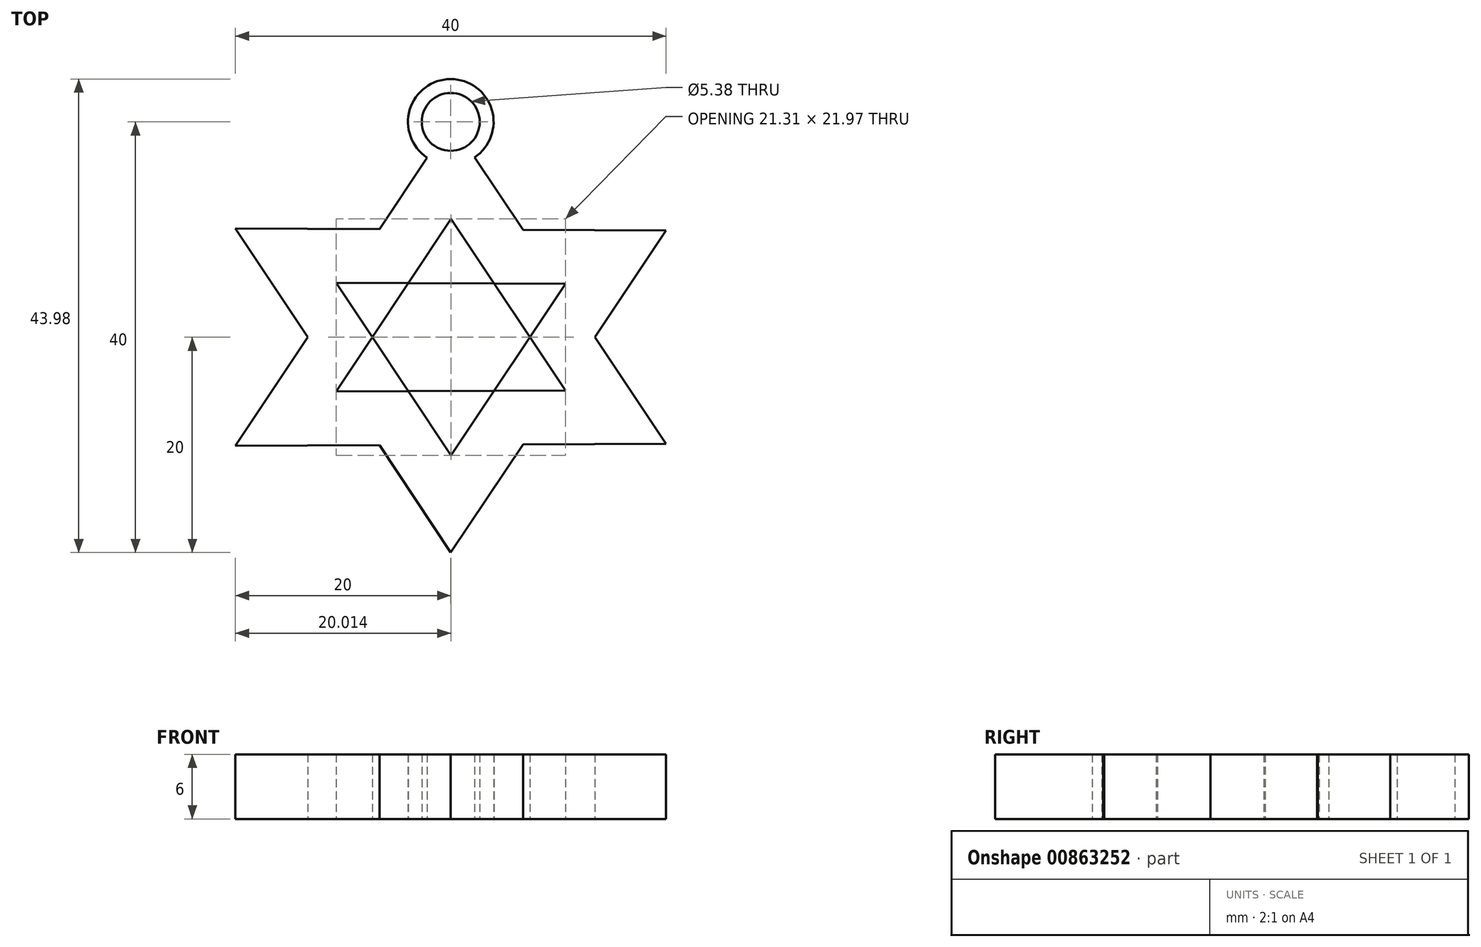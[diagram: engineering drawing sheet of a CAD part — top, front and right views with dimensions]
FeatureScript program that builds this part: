
annotation { "Feature Type Name" : "Feature", "Feature Type Description" : "" }
export const myFeature = defineFeature(function(context is Context, id is Id, definition is map)
    precondition{}
    {
        {
            var Q0;
            Q0=qCreatedBy(makeId("Top.planeOp"),FACE);
            var sketch = newSketch(context, id + "F0", { "sketchPlane" : qUnion([Q0])});
            skLineSegment(sketch, "E0", {"start": v(-20, 10.1) * mm, "end": v(20, 9.9) * mm});
            skLineSegment(sketch, "E1", {"start": v(-20, -10.1) * mm, "end": v(20, -9.9) * mm});
            skLineSegment(sketch, "E2", {"start": v(-1.49, 17.76) * mm, "end": v(-20, -10.1) * mm});
            skLineSegment(sketch, "E3", {"start": v(20, -9.9) * mm, "end": v(1.5, 17.77) * mm});
            skLineSegment(sketch, "E4", {"start": v(0, -20) * mm, "end": v(20, 9.9) * mm});
            skLineSegment(sketch, "E5", {"start": v(-20, 10.1) * mm, "end": v(0, -20) * mm});
            skLineSegment(sketch, "E6.0", {"start": v(-10.64, 5.05) * mm, "end": v(10.67, 4.95) * mm});
            skLineSegment(sketch, "E6.1", {"start": v(-10.64, 5.05) * mm, "end": v(0.01, -10.99) * mm});
            skLineSegment(sketch, "E6.2", {"start": v(0.01, -10.99) * mm, "end": v(10.67, 4.95) * mm});
            skLineSegment(sketch, "E7.0", {"start": v(10.67, -4.95) * mm, "end": v(0.01, 10.99) * mm});
            skLineSegment(sketch, "E7.1", {"start": v(-10.64, -5.05) * mm, "end": v(10.67, -4.95) * mm});
            skLineSegment(sketch, "E7.2", {"start": v(0.01, 10.99) * mm, "end": v(-10.64, -5.05) * mm});
            skCircle(sketch, "E8", {"center": v(0, 20) * mm, "radius": 3.98 * mm});
            skCircle(sketch, "E9", {"center": v(0, 20) * mm, "radius": 2.69 * mm});
            skSolve(sketch);
        }
        {
            var Q0;
            {var subQ0=sQuery(id+"F0.wireOp",EDGE,"E5");var subQ7=sQuery(id+"F0.wireOp",EDGE,"E0");var subQ10=makeQuery(id+"F0.imprint","INTERSECT",VERTEX,{"derivedFrom":[subQ7,subQ0]});Q0=makeQuery(id+"F0.imprint","IMPRINT",FACE,{"disambiguationData":[TD([[makeQuery(id+"F0.imprint","IMPRINT",EDGE,{"disambiguationData":[TD([[subQ10,-1.0]])],"derivedFrom":subQ7}),-1.0]])]});}
            var Q1;
            {var subQ1=sQuery(id+"F0.wireOp",EDGE,"E2");var subQ3=sQuery(id+"F0.wireOp",EDGE,"E0");var subQ5=makeQuery(id+"F0.imprint","INTERSECT",VERTEX,{"derivedFrom":[subQ3,subQ1]});Q1=makeQuery(id+"F0.imprint","IMPRINT",FACE,{"disambiguationData":[TD([[makeQuery(id+"F0.imprint","IMPRINT",EDGE,{"disambiguationData":[TD([[subQ5,-1.0]])],"derivedFrom":subQ3}),1.0]])]});}
            var Q2;
            {var subQ1=sQuery(id+"F0.wireOp",EDGE,"E0");var subQ5=sQuery(id+"F0.wireOp",EDGE,"E4");var subQ9=makeQuery(id+"F0.imprint","INTERSECT",VERTEX,{"derivedFrom":[subQ1,subQ5]});Q2=makeQuery(id+"F0.imprint","IMPRINT",FACE,{"disambiguationData":[TD([[makeQuery(id+"F0.imprint","IMPRINT",EDGE,{"disambiguationData":[TD([[subQ9,1.0]])],"derivedFrom":subQ1}),-1.0]])]});}
            var Q3;
            {var subQ0=sQuery(id+"F0.wireOp",EDGE,"E3");var subQ1=sQuery(id+"F0.wireOp",EDGE,"E0");var subQ2=makeQuery(id+"F0.imprint","INTERSECT",VERTEX,{"derivedFrom":[subQ1,subQ0]});Q3=makeQuery(id+"F0.imprint","IMPRINT",FACE,{"disambiguationData":[TD([[makeQuery(id+"F0.imprint","IMPRINT",EDGE,{"disambiguationData":[TD([[subQ2,1.0]])],"derivedFrom":subQ1}),-1.0]])]});}
            var Q4;
            {var subQ0=sQuery(id+"F0.wireOp",EDGE,"E4");var subQ1=sQuery(id+"F0.wireOp",EDGE,"E3");var subQ2=makeQuery(id+"F0.imprint","INTERSECT",VERTEX,{"derivedFrom":[subQ1,subQ0]});Q4=makeQuery(id+"F0.imprint","IMPRINT",FACE,{"disambiguationData":[TD([[makeQuery(id+"F0.imprint","IMPRINT",EDGE,{"disambiguationData":[TD([[subQ2,-1.0]])],"derivedFrom":subQ1}),1.0]])]});}
            var Q5;
            {var subQ1=sQuery(id+"F0.wireOp",EDGE,"E3");var subQ7=sQuery(id+"F0.wireOp",EDGE,"E1");var subQ10=makeQuery(id+"F0.imprint","INTERSECT",VERTEX,{"derivedFrom":[subQ7,subQ1]});Q5=makeQuery(id+"F0.imprint","IMPRINT",FACE,{"disambiguationData":[TD([[makeQuery(id+"F0.imprint","IMPRINT",EDGE,{"disambiguationData":[TD([[subQ10,1.0]])],"derivedFrom":subQ7}),1.0]])]});}
            var Q6;
            {var subQ0=sQuery(id+"F0.wireOp",EDGE,"E4");var subQ1=sQuery(id+"F0.wireOp",EDGE,"E1");var subQ2=makeQuery(id+"F0.imprint","INTERSECT",VERTEX,{"derivedFrom":[subQ1,subQ0]});Q6=makeQuery(id+"F0.imprint","IMPRINT",FACE,{"disambiguationData":[TD([[makeQuery(id+"F0.imprint","IMPRINT",EDGE,{"disambiguationData":[TD([[subQ2,1.0]])],"derivedFrom":subQ1}),1.0]])]});}
            var Q7;
            {var subQ0=sQuery(id+"F0.wireOp",EDGE,"E5");var subQ3=sQuery(id+"F0.wireOp",EDGE,"E1");var subQ4=makeQuery(id+"F0.imprint","INTERSECT",VERTEX,{"derivedFrom":[subQ3,subQ0]});Q7=makeQuery(id+"F0.imprint","IMPRINT",FACE,{"disambiguationData":[TD([[makeQuery(id+"F0.imprint","IMPRINT",EDGE,{"disambiguationData":[TD([[subQ4,-1.0]])],"derivedFrom":subQ3}),-1.0]])]});}
            var Q8;
            {var subQ1=sQuery(id+"F0.wireOp",EDGE,"E1");var subQ7=sQuery(id+"F0.wireOp",EDGE,"E2");var subQ10=makeQuery(id+"F0.imprint","INTERSECT",VERTEX,{"derivedFrom":[subQ1,subQ7]});Q8=makeQuery(id+"F0.imprint","IMPRINT",FACE,{"disambiguationData":[TD([[makeQuery(id+"F0.imprint","IMPRINT",EDGE,{"disambiguationData":[TD([[subQ10,-1.0]])],"derivedFrom":subQ1}),1.0]])]});}
            var Q9;
            {var subQ0=sQuery(id+"F0.wireOp",EDGE,"E5");var subQ1=sQuery(id+"F0.wireOp",EDGE,"E1");var subQ2=makeQuery(id+"F0.imprint","INTERSECT",VERTEX,{"derivedFrom":[subQ1,subQ0]});Q9=makeQuery(id+"F0.imprint","IMPRINT",FACE,{"disambiguationData":[TD([[makeQuery(id+"F0.imprint","IMPRINT",EDGE,{"disambiguationData":[TD([[subQ2,-1.0]])],"derivedFrom":subQ1}),1.0]])]});}
            var Q10;
            {var subQ0=sQuery(id+"F0.wireOp",EDGE,"E5");var subQ1=sQuery(id+"F0.wireOp",EDGE,"E2");var subQ2=makeQuery(id+"F0.imprint","INTERSECT",VERTEX,{"derivedFrom":[subQ1,subQ0]});Q10=makeQuery(id+"F0.imprint","IMPRINT",FACE,{"disambiguationData":[TD([[makeQuery(id+"F0.imprint","IMPRINT",EDGE,{"disambiguationData":[TD([[subQ2,1.0]])],"derivedFrom":subQ1}),1.0]])]});}
            var Q11;
            {var subQ0=sQuery(id+"F0.wireOp",EDGE,"E2");var subQ1=sQuery(id+"F0.wireOp",EDGE,"E0");var subQ2=makeQuery(id+"F0.imprint","INTERSECT",VERTEX,{"derivedFrom":[subQ1,subQ0]});Q11=makeQuery(id+"F0.imprint","IMPRINT",FACE,{"disambiguationData":[TD([[makeQuery(id+"F0.imprint","IMPRINT",EDGE,{"disambiguationData":[TD([[subQ2,-1.0]])],"derivedFrom":subQ1}),-1.0]])]});}
            var Q12;
            {var subQ1=sQuery(id+"F0.wireOp",EDGE,"E6.0");var subQ7=sQuery(id+"F0.wireOp",EDGE,"E7.2");var subQ11=makeQuery(id+"F0.imprint","INTERSECT",VERTEX,{"derivedFrom":[subQ1,subQ7]});Q12=makeQuery(id+"F0.imprint","IMPRINT",FACE,{"disambiguationData":[TD([[makeQuery(id+"F0.imprint","IMPRINT",EDGE,{"disambiguationData":[TD([[subQ11,-1.0]])],"derivedFrom":subQ1}),-1.0]])]});}
            var Q13;
            {var subQ0=sQuery(id+"F0.wireOp",EDGE,"E9");var subQ1=sQuery(id+"F0.wireOp",EDGE,"E2");var subQ2=makeQuery(id+"F0.imprint","INTERSECT",VERTEX,{"derivedFrom":[subQ1,subQ0]});Q13=makeQuery(id+"F0.imprint","IMPRINT",FACE,{"disambiguationData":[TD([[makeQuery(id+"F0.imprint","IMPRINT",EDGE,{"disambiguationData":[TD([[subQ2,-1.0]])],"derivedFrom":subQ1}),-1.0]])]});}
            var Q14;
            {var subQ0=sQuery(id+"F0.wireOp",EDGE,"E9");var subQ1=sQuery(id+"F0.wireOp",EDGE,"E2");var subQ2=makeQuery(id+"F0.imprint","INTERSECT",VERTEX,{"derivedFrom":[subQ1,subQ0]});Q14=makeQuery(id+"F0.imprint","IMPRINT",FACE,{"disambiguationData":[TD([[makeQuery(id+"F0.imprint","IMPRINT",EDGE,{"disambiguationData":[TD([[subQ2,-1.0]])],"derivedFrom":subQ1}),1.0]])]});}
            extrude(context, id + "F1", {"entities" : qUnion([Q0, Q1, Q2, Q3, Q4, Q5, Q6, Q7, Q8, Q9, Q10, Q11, Q12, Q13, Q14]), "depth" : 6 * mm, "offsetDistance" : 25 * mm});
        }
    });
